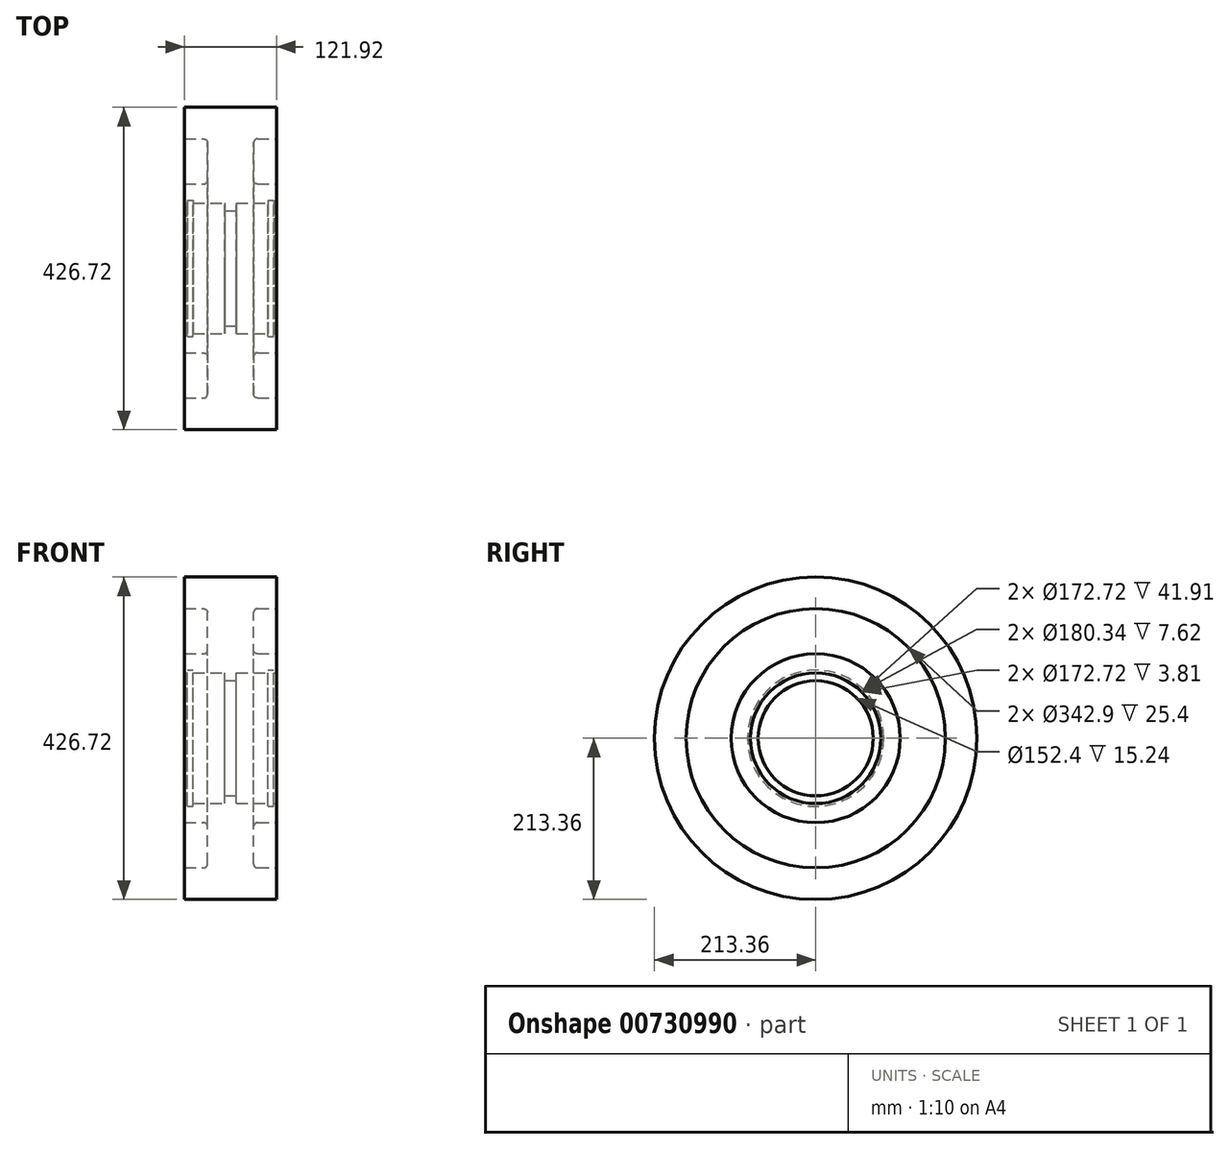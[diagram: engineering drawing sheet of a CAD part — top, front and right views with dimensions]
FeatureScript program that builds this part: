
annotation { "Feature Type Name" : "Feature", "Feature Type Description" : "" }
export const myFeature = defineFeature(function(context is Context, id is Id, definition is map)
    precondition{}
    {
        {
            var Q0;
            Q0=qCreatedBy(makeId("Front.planeOp"),FACE);
            var sketch = newSketch(context, id + "F0", { "sketchPlane" : qUnion([Q0])});
            skLineSegment(sketch, "E0", {"start": v(0, 213.36) * mm, "end": v(0, 0) * mm});
            skLineSegment(sketch, "E1", {"start": v(0, 0) * mm, "end": v(0, 213.36) * mm, "construction": true});
            skLineSegment(sketch, "E2", {"start": v(-60.96, 111.76) * mm, "end": v(-60.96, 86.36) * mm, "construction": true});
            skLineSegment(sketch, "E3", {"start": v(-60.96, 86.36) * mm, "end": v(-60.96, 111.76) * mm});
            skLineSegment(sketch, "E4", {"start": v(-60.96, 213.36) * mm, "end": v(0, 213.36) * mm});
            skLineSegment(sketch, "E5", {"start": v(0, 0) * mm, "end": v(-60.96, 0) * mm, "construction": true});
            skLineSegment(sketch, "E6", {"start": v(-60.96, 86.36) * mm, "end": v(-57.15, 86.36) * mm});
            skLineSegment(sketch, "E7", {"start": v(-57.15, 86.36) * mm, "end": v(-57.15, 90.17) * mm});
            skLineSegment(sketch, "E8", {"start": v(-57.15, 90.17) * mm, "end": v(-49.53, 90.17) * mm});
            skLineSegment(sketch, "E9", {"start": v(-49.53, 90.17) * mm, "end": v(-49.53, 86.36) * mm});
            skLineSegment(sketch, "E10", {"start": v(-49.53, 86.36) * mm, "end": v(-7.62, 86.36) * mm});
            skLineSegment(sketch, "E11", {"start": v(-7.62, 86.36) * mm, "end": v(-7.62, 76.2) * mm});
            skLineSegment(sketch, "E12", {"start": v(-7.62, 76.2) * mm, "end": v(0, 76.2) * mm});
            skLineSegment(sketch, "E13", {"start": v(-60.96, 171.45) * mm, "end": v(-35.56, 171.45) * mm});
            skLineSegment(sketch, "E14", {"start": v(-30.48, 166.37) * mm, "end": v(-30.48, 116.84) * mm});
            skLineSegment(sketch, "E15", {"start": v(-35.56, 111.76) * mm, "end": v(-60.96, 111.76) * mm});
            skLineSegment(sketch, "E16.trimOffspring", {"start": v(-60.96, 171.45) * mm, "end": v(-60.96, 213.36) * mm});
            skPoint(sketch, "E17.visualSharp", {"position": v(-30.48, 171.45) * mm});
            skArc(sketch, "E17.filletArc", {"start": v(-30.48, 166.37) * mm, "mid": v(-31.97, 169.96) * mm, "end": v(-35.56, 171.45) * mm});
            skPoint(sketch, "E18.visualSharp", {"position": v(-30.48, 111.76) * mm});
            skArc(sketch, "E18.filletArc", {"start": v(-35.56, 111.76) * mm, "mid": v(-31.97, 113.25) * mm, "end": v(-30.48, 116.84) * mm});
            skLineSegment(sketch, "E19.MirrorCS", {"start": v(60.96, 213.36) * mm, "end": v(0, 213.36) * mm});
            skLineSegment(sketch, "E20.MirrorCS", {"start": v(60.96, 171.45) * mm, "end": v(60.96, 213.36) * mm});
            skLineSegment(sketch, "E21.MirrorCS", {"start": v(60.96, 171.45) * mm, "end": v(35.56, 171.45) * mm});
            skArc(sketch, "E22.MirrorCS", {"start": v(30.48, 166.37) * mm, "mid": v(31.97, 169.96) * mm, "end": v(35.56, 171.45) * mm});
            skLineSegment(sketch, "E23.MirrorCS", {"start": v(30.48, 166.37) * mm, "end": v(30.48, 116.84) * mm});
            skArc(sketch, "E24.MirrorCS", {"start": v(35.56, 111.76) * mm, "mid": v(31.97, 113.25) * mm, "end": v(30.48, 116.84) * mm});
            skLineSegment(sketch, "E25.MirrorCS", {"start": v(35.56, 111.76) * mm, "end": v(60.96, 111.76) * mm});
            skLineSegment(sketch, "E26.MirrorCS", {"start": v(60.96, 111.76) * mm, "end": v(60.96, 86.36) * mm});
            skLineSegment(sketch, "E27.MirrorCS", {"start": v(60.96, 86.36) * mm, "end": v(57.15, 86.36) * mm});
            skLineSegment(sketch, "E28.MirrorCS", {"start": v(57.15, 90.17) * mm, "end": v(49.53, 90.17) * mm});
            skLineSegment(sketch, "E29.MirrorCS", {"start": v(49.53, 86.36) * mm, "end": v(7.62, 86.36) * mm});
            skLineSegment(sketch, "E30.MirrorCS", {"start": v(7.62, 86.36) * mm, "end": v(7.62, 76.2) * mm});
            skLineSegment(sketch, "E31.MirrorCS", {"start": v(7.62, 76.2) * mm, "end": v(0, 76.2) * mm});
            skLineSegment(sketch, "E32.MirrorCS", {"start": v(57.15, 86.36) * mm, "end": v(57.15, 90.17) * mm});
            skLineSegment(sketch, "E33.MirrorCS", {"start": v(49.53, 90.17) * mm, "end": v(49.53, 86.36) * mm});
            skSolve(sketch);
        }
        {
            var Q0;
            Q0=makeQuery(id+"F0.imprint","IMPRINT",FACE,{"disambiguationData":[TD([[makeQuery(id+"F0.imprint","IMPRINT",EDGE,{"derivedFrom":sQuery(id+"F0.wireOp",EDGE,"E3")}),-1.0]])]});
            var Q1;
            {var subQ0=sQuery(id+"F0.wireOp",EDGE,"E19.MirrorCS");Q1=makeQuery(id+"F0.imprint","IMPRINT",FACE,{"disambiguationData":[TD([[makeQuery(id+"F0.imprint","IMPRINT",EDGE,{"derivedFrom":subQ0}),1.0]])]});}
            var Q2;
            Q2=sQuery(id+"F0.wireOp",EDGE,"E5");
            revolve(context, id + "F1", {"surfaceOperationType" : NewSurfaceOperationType.NEW, "entities" : qUnion([Q0, Q1]), "axis" : qUnion([Q2]), "revolveType" : RevolveType.FULL});
        }
    });
